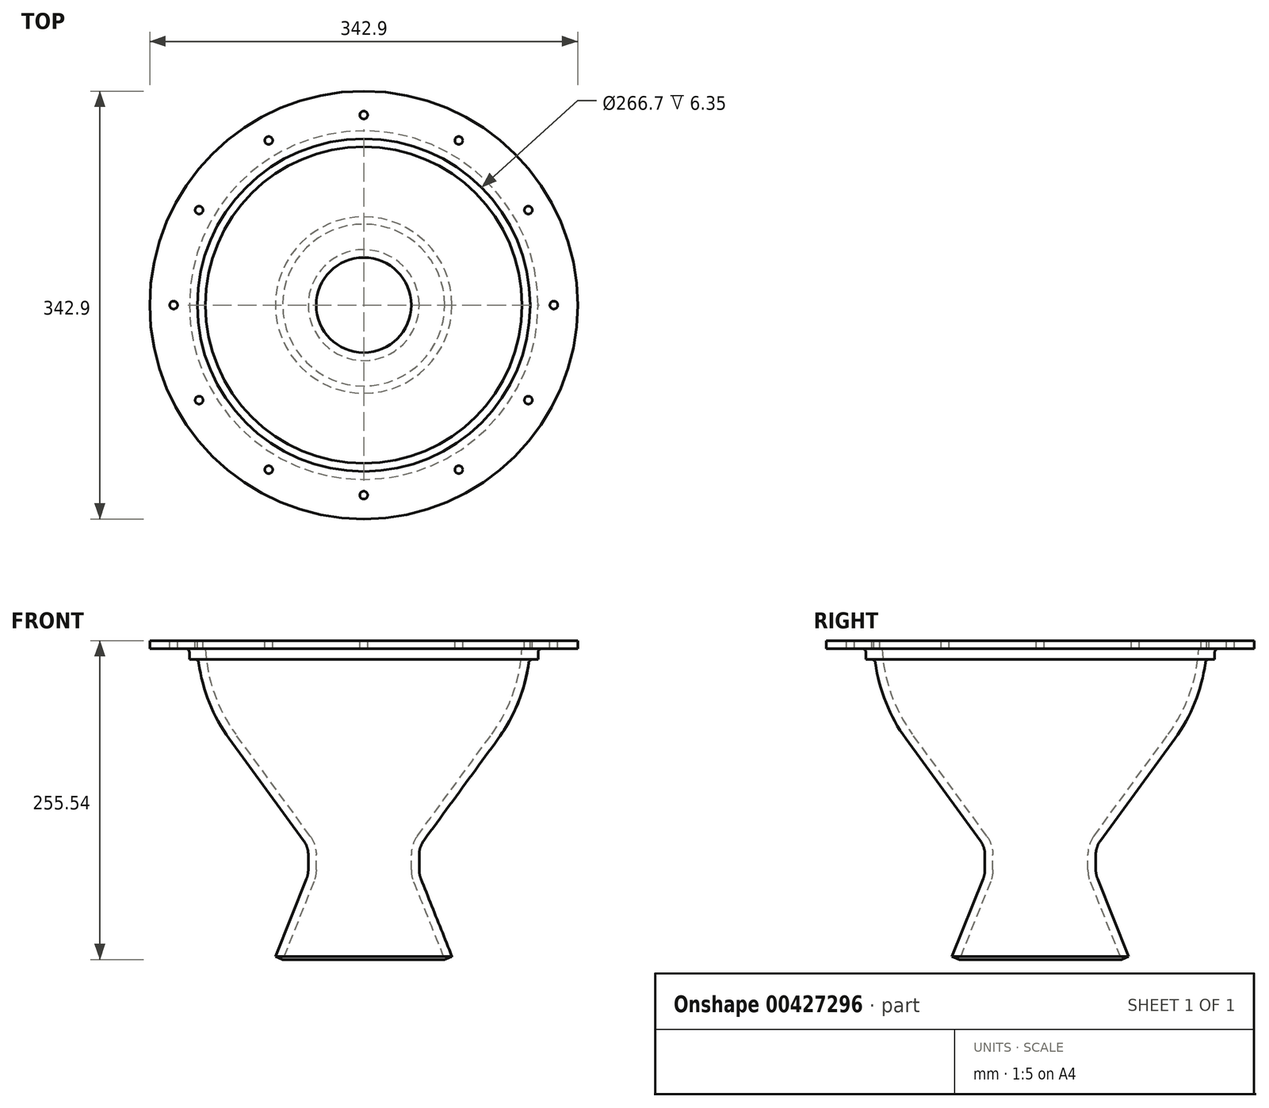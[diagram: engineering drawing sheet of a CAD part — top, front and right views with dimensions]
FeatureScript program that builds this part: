
annotation { "Feature Type Name" : "Feature", "Feature Type Description" : "" }
export const myFeature = defineFeature(function(context is Context, id is Id, definition is map)
    precondition{}
    {
        {
            var Q0;
            Q0=qCreatedBy(makeId("Front.planeOp"),FACE);
            var sketch = newSketch(context, id + "F0", { "sketchPlane" : qUnion([Q0])});
            skArc(sketch, "E0", {"start": v(127, 0) * mm, "mid": v(89.8, 89.8) * mm, "end": v(0, 127) * mm});
            skLineSegment(sketch, "E1", {"start": v(127, 0) * mm, "end": v(127, -6.35) * mm});
            skLineSegment(sketch, "E2", {"start": v(127, -6.35) * mm, "end": v(133.35, -6.35) * mm});
            skLineSegment(sketch, "E3", {"start": v(133.35, -6.35) * mm, "end": v(133.35, 0) * mm});
            skLineSegment(sketch, "E4", {"start": v(133.35, 0) * mm, "end": v(133.35, 0) * mm});
            skLineSegment(sketch, "E5", {"start": v(171.45, 6.35) * mm, "end": v(133.2, 6.35) * mm});
            skArc(sketch, "E6.0", {"start": v(133.2, 6.35) * mm, "mid": v(92.02, 96.51) * mm, "end": v(0, 133.35) * mm});
            skLineSegment(sketch, "E7", {"start": v(0, 127) * mm, "end": v(0, 133.35) * mm});
            skPoint(sketch, "E8.end.orphan", {"position": v(-133.35, 0) * mm});
            skLineSegment(sketch, "E9", {"start": v(0, 0) * mm, "end": v(0, 26.63) * mm, "construction": true});
            skLineSegment(sketch, "E10", {"start": v(133.35, 0) * mm, "end": v(171.45, 0) * mm});
            skLineSegment(sketch, "E11", {"start": v(171.45, 0) * mm, "end": v(171.45, 6.35) * mm});
            skSolve(sketch);
        }
        {
            var Q0;
            Q0=makeQuery(id+"F0.imprint","IMPRINT",FACE,{"disambiguationData":[TD([[makeQuery(id+"F0.imprint","IMPRINT",EDGE,{"derivedFrom":sQuery(id+"F0.wireOp",EDGE,"E0")}),-1.0]])]});
            var Q1;
            Q1=sQuery(id+"F0.wireOp",EDGE,"E9");
            revolve(context, id + "F1", {"entities" : qUnion([Q0]), "axis" : qUnion([Q1]), "revolveType" : RevolveType.FULL});
        }
        {
            var Q0;
            Q0=qCreatedBy(makeId("Front.planeOp"),FACE);
            var sketch = newSketch(context, id + "F2", { "sketchPlane" : qUnion([Q0])});
            skLineSegment(sketch, "E12", {"start": v(0, 0) * mm, "end": v(0, 155.52) * mm});
            skLineSegment(sketch, "E13", {"start": v(0, 0) * mm, "end": v(109.2, 109.2) * mm});
            skSolve(sketch);
        }
        {
            var Q0;
            Q0=qCreatedBy(makeId("Top.planeOp"),FACE);
            var Q1;
            Q1=sQuery(id+"F2.wireOp",EDGE,"E13");
            cPlane(context, id + "F3", {"entities" : qUnion([Q0, Q1]), "cplaneType" : CPlaneType.LINE_ANGLE, "offset" : 25.4 * mm, "angle" : 0 * degree, "oppositeDirection" : true, "width" : 152.4 * mm, "height" : 152.4 * mm});
        }
        {
            var Q0;
            Q0=qCreatedBy(makeId("Front.planeOp"),FACE);
            var sketch = newSketch(context, id + "F4", { "sketchPlane" : qUnion([Q0])});
            skArc(sketch, "E14", {"start": v(98.33, 80.37) * mm, "mid": v(94.19, 85.2) * mm, "end": v(89.8, 89.8) * mm});
            skLineSegment(sketch, "E15", {"start": v(89.8, 89.8) * mm, "end": v(94.3, 94.3) * mm});
            skLineSegment(sketch, "E16", {"start": v(0, 0) * mm, "end": v(0, 157.57) * mm});
            skLineSegment(sketch, "E17.0", {"start": v(98.33, 80.37) * mm, "end": v(100.78, 82.81) * mm});
            skLineSegment(sketch, "E18", {"start": v(103.02, 80.57) * mm, "end": v(100.78, 82.81) * mm});
            skLineSegment(sketch, "E19", {"start": v(103.02, 80.57) * mm, "end": v(110.36, 87.91) * mm});
            skPoint(sketch, "E20.trimOffspring.end.orphan", {"position": v(-133.2, 6.35) * mm});
            skPoint(sketch, "E21.trimOffspring.end.orphan", {"position": v(-127, 0) * mm});
            skPoint(sketch, "E22.start.orphan", {"position": v(133.2, 6.35) * mm});
            skLineSegment(sketch, "E23", {"start": v(94.3, 94.3) * mm, "end": v(110.36, 87.91) * mm});
            skPoint(sketch, "E24.orphan", {"position": v(127, 0) * mm});
            skSolve(sketch);
        }
        {
            var Q0;
            Q0=makeQuery(id+"F4.imprint","IMPRINT",FACE,{"disambiguationData":[TD([[makeQuery(id+"F4.imprint","IMPRINT",EDGE,{"derivedFrom":sQuery(id+"F4.wireOp",EDGE,"E14")}),-1.0]])]});
            var Q1;
            Q1=sQuery(id+"F4.wireOp",EDGE,"E15");
            revolve(context, id + "F5", {"operationType" : NewBodyOperationType.REMOVE, "entities" : qUnion([Q0]), "axis" : qUnion([Q1]), "revolveType" : RevolveType.FULL, "oppositeDirection" : true});
        }
        {
            var Q0;
            Q0=qCreatedBy(makeId("Front.planeOp"),FACE);
            var sketch = newSketch(context, id + "F6", { "sketchPlane" : qUnion([Q0])});
            skLineSegment(sketch, "E25", {"start": v(0, 127) * mm, "end": v(0, 133.35) * mm});
            skArc(sketch, "E26", {"start": v(0, 133.35) * mm, "mid": v(-3.97, 133.3) * mm, "end": v(-7.94, 133.11) * mm});
            skArc(sketch, "E27", {"start": v(-104.85, 82.4) * mm, "mid": v(-124.95, 46.58) * mm, "end": v(-133.2, 6.35) * mm});
            skArc(sketch, "E28", {"start": v(133.2, 6.35) * mm, "mid": v(124.95, 46.58) * mm, "end": v(104.85, 82.4) * mm});
            skArc(sketch, "E29", {"start": v(0, 127) * mm, "mid": v(-3.97, 126.94) * mm, "end": v(-7.94, 126.75) * mm});
            skArc(sketch, "E30", {"start": v(-98.33, 80.37) * mm, "mid": v(-119.62, 42.67) * mm, "end": v(-127, 0) * mm});
            skArc(sketch, "E31", {"start": v(127, 0) * mm, "mid": v(119.62, 42.67) * mm, "end": v(98.33, 80.37) * mm});
            skLineSegment(sketch, "E32.0", {"start": v(-7.94, 126.75) * mm, "end": v(-7.94, 133.11) * mm});
            skPoint(sketch, "E33.orphan", {"position": v(80.37, 98.33) * mm});
            skPoint(sketch, "E34.orphan", {"position": v(82.4, 104.85) * mm});
            skPoint(sketch, "E35.orphan", {"position": v(-82.4, 104.85) * mm});
            skPoint(sketch, "E36.orphan", {"position": v(-80.37, 98.33) * mm});
            skSolve(sketch);
        }
        {
            var Q0;
            Q0=makeQuery(id+"F6.imprint","IMPRINT",FACE,{"disambiguationData":[TD([[makeQuery(id+"F6.imprint","IMPRINT",EDGE,{"derivedFrom":sQuery(id+"F6.wireOp",EDGE,"E25")}),1.0]])]});
            var Q1;
            Q1=sQuery(id+"F6.wireOp",EDGE,"E25");
            revolve(context, id + "F7", {"operationType" : NewBodyOperationType.REMOVE, "entities" : qUnion([Q0]), "axis" : qUnion([Q1]), "revolveType" : RevolveType.FULL, "oppositeDirection" : true});
        }
        {
            var Q0;
            Q0=makeQuery(id+"F1.opRevolve","SWEPT_FACE",FACE,{"disambiguationData":[OSD([sQuery(id+"F0.wireOp",EDGE,"E5")])]});
            var sketch = newSketch(context, id + "F8", { "sketchPlane" : qUnion([Q0])});
            skLineSegment(sketch, "E37", {"start": v(0, -133.2) * mm, "end": v(0, -171.45) * mm, "construction": true});
            skCircle(sketch, "E38", {"center": v(0, 0) * mm, "radius": 171.45 * mm, "construction": true});
            skCircle(sketch, "E39", {"center": v(0, 0) * mm, "radius": 133.2 * mm, "construction": true});
            skPoint(sketch, "E40", {"position": v(0, -152.32) * mm});
            skSolve(sketch);
        }
        {
            var Q0;
            Q0=sQuery(id+"F8.wireOp",VERTEX,"E40");
            var Q1;
            Q1=makeQuery(id+"F1.opRevolve","SWEPT_BODY",BODY,{"disambiguationData":[OSD([sQuery(id+"F0.wireOp",EDGE,"E0"),sQuery(id+"F0.wireOp",EDGE,"E1"),sQuery(id+"F0.wireOp",EDGE,"E2"),sQuery(id+"F0.wireOp",EDGE,"E3"),sQuery(id+"F0.wireOp",EDGE,"E5"),sQuery(id+"F0.wireOp",EDGE,"E6.0"),sQuery(id+"F0.wireOp",EDGE,"E7"),sQuery(id+"F0.wireOp",EDGE,"E10"),sQuery(id+"F0.wireOp",EDGE,"E11")])]});
            hole(context, id + "F9", {"style" : HoleStyle.SIMPLE, "endStyle" : HoleEndStyle.THROUGH, "holeDiameter" : 6.35 * mm, "isTappedThrough" : true, "tappedDepth" : 12.7 * mm, "tapClearance" : 3, "locations" : qUnion([Q0]), "scope" : qUnion([Q1])});
        }
        {
            var Q0;
            Q0=qCreatedBy(makeId("Front.planeOp"),FACE);
            var sketch = newSketch(context, id + "F10", { "sketchPlane" : qUnion([Q0])});
            skLineSegment(sketch, "E41", {"start": v(-171.45, 0) * mm, "end": v(-133.35, 0) * mm});
            skLineSegment(sketch, "E42", {"start": v(-133.35, -6.35) * mm, "end": v(-126.84, -6.35) * mm});
            skLineSegment(sketch, "E43", {"start": v(-133.35, 0) * mm, "end": v(-133.35, -6.35) * mm});
            skArc(sketch, "E44", {"start": v(-126.84, -6.35) * mm, "mid": v(-119.72, -42.38) * mm, "end": v(-102.59, -74.87) * mm});
            skLineSegment(sketch, "E45", {"start": v(-171.45, 0) * mm, "end": v(-171.45, -6.35) * mm});
            skPoint(sketch, "E46.end.orphan", {"position": v(-133.35, 0) * mm});
            skPoint(sketch, "E46.start.orphan", {"position": v(-149.15, 0) * mm});
            skPoint(sketch, "E47.orphan", {"position": v(-155.5, 0) * mm});
            skPoint(sketch, "E48.end.orphan", {"position": v(-80.37, 98.33) * mm});
            skPoint(sketch, "E48.start.orphan", {"position": v(-7.94, 126.75) * mm});
            skPoint(sketch, "E49.end.orphan", {"position": v(7.94, 126.75) * mm});
            skPoint(sketch, "E49.start.orphan", {"position": v(80.37, 98.33) * mm});
            skPoint(sketch, "E50.end.orphan", {"position": v(98.33, 80.37) * mm});
            skPoint(sketch, "E50.start.orphan", {"position": v(127, 0) * mm});
            skPoint(sketch, "E51.end.orphan", {"position": v(127, -6.35) * mm});
            skPoint(sketch, "E52.end.orphan", {"position": v(133.35, -6.35) * mm});
            skPoint(sketch, "E53.end.orphan", {"position": v(133.35, 0) * mm});
            skPoint(sketch, "E54.end.orphan", {"position": v(149.15, 0) * mm});
            skPoint(sketch, "E55.end.orphan", {"position": v(171.45, 0) * mm});
            skPoint(sketch, "E55.start.orphan", {"position": v(155.5, 0) * mm});
            skPoint(sketch, "E56.orphan", {"position": v(-127, 0) * mm});
            skPoint(sketch, "E57.orphan", {"position": v(-98.33, 80.37) * mm});
            skPoint(sketch, "E58.start.orphan", {"position": v(-127, -6.35) * mm});
            skLineSegment(sketch, "E59", {"start": v(-38.1, -183.74) * mm, "end": v(-38.1, -171.51) * mm});
            skPoint(sketch, "E60.visualSharp", {"position": v(-31.75, -122.97) * mm});
            skPoint(sketch, "E61.visualSharp", {"position": v(-44.5, -173.77) * mm});
            skPoint(sketch, "E62.start.orphan", {"position": v(-31.75, -186.47) * mm});
            skLineSegment(sketch, "E63", {"start": v(-42.98, -156.54) * mm, "end": v(-102.59, -74.87) * mm});
            skLineSegment(sketch, "E64", {"start": v(-39.92, -193.17) * mm, "end": v(-64.86, -255.54) * mm});
            skPoint(sketch, "E65.start.orphan", {"position": v(-31.75, -249.97) * mm});
            skPoint(sketch, "E66.visualSharp", {"position": v(-38.1, -163.23) * mm});
            skArc(sketch, "E66.filletArc", {"start": v(-38.1, -171.51) * mm, "mid": v(-39.35, -163.64) * mm, "end": v(-42.98, -156.54) * mm});
            skPoint(sketch, "E67.visualSharp", {"position": v(-38.1, -188.63) * mm});
            skArc(sketch, "E67.filletArc", {"start": v(-39.92, -193.17) * mm, "mid": v(-38.56, -188.54) * mm, "end": v(-38.1, -183.74) * mm});
            skPoint(sketch, "E68.0.end.orphan", {"position": v(6.35, -67.27) * mm});
            skLineSegment(sketch, "E69.0", {"start": v(-45.81, -190.82) * mm, "end": v(-70.76, -253.18) * mm});
            skArc(sketch, "E69.1", {"start": v(-45.81, -190.82) * mm, "mid": v(-44.8, -187.34) * mm, "end": v(-44.45, -183.74) * mm});
            skArc(sketch, "E69.2", {"start": v(-132.16, -17.8) * mm, "mid": v(-123.73, -49.73) * mm, "end": v(-107.72, -78.6) * mm});
            skLineSegment(sketch, "E69.3", {"start": v(-48.11, -160.28) * mm, "end": v(-107.72, -78.6) * mm});
            skArc(sketch, "E69.4", {"start": v(-44.45, -171.51) * mm, "mid": v(-45.39, -165.6) * mm, "end": v(-48.11, -160.28) * mm});
            skLineSegment(sketch, "E69.5", {"start": v(-44.45, -183.74) * mm, "end": v(-44.45, -171.51) * mm});
            skLineSegment(sketch, "E70", {"start": v(-64.86, -255.54) * mm, "end": v(-70.76, -253.18) * mm});
            skLineSegment(sketch, "E71", {"start": v(-171.45, -6.35) * mm, "end": v(-142.88, -6.35) * mm});
            skLineSegment(sketch, "E72", {"start": v(-139.7, -9.52) * mm, "end": v(-139.7, -15.06) * mm});
            skLineSegment(sketch, "E73", {"start": v(-139.7, -15.06) * mm, "end": v(-135.3, -15.06) * mm});
            skPoint(sketch, "E74.visualSharp", {"position": v(-139.7, -6.35) * mm});
            skArc(sketch, "E74.filletArc", {"start": v(-139.7, -9.52) * mm, "mid": v(-140.63, -7.28) * mm, "end": v(-142.88, -6.35) * mm});
            skPoint(sketch, "E75.visualSharp", {"position": v(-132.5, -15.06) * mm});
            skArc(sketch, "E75.filletArc", {"start": v(-132.16, -17.8) * mm, "mid": v(-133.21, -15.84) * mm, "end": v(-135.3, -15.06) * mm});
            skLineSegment(sketch, "E76", {"start": v(0, 0) * mm, "end": v(0, -104.7) * mm});
            skSolve(sketch);
        }
        {
            var Q0;
            Q0=makeQuery(id+"F10.imprint","IMPRINT",FACE,{"disambiguationData":[TD([[makeQuery(id+"F10.imprint","IMPRINT",EDGE,{"derivedFrom":sQuery(id+"F10.wireOp",EDGE,"E41")}),-1.0]])]});
            var Q1;
            Q1=sQuery(id+"F10.wireOp",EDGE,"E76");
            revolve(context, id + "F11", {"entities" : qUnion([Q0]), "axis" : qUnion([Q1]), "revolveType" : RevolveType.FULL});
        }
        {
            var Q0;
            Q0=makeQuery(id+"F11.opRevolve","SWEPT_FACE",FACE,{"disambiguationData":[OSD([sQuery(id+"F10.wireOp",EDGE,"E41")])]});
            var sketch = newSketch(context, id + "F12", { "sketchPlane" : qUnion([Q0])});
            skCircle(sketch, "E77.0", {"center": v(131.92, -76.16) * mm, "radius": 3.17 * mm});
            skCircle(sketch, "E78.0", {"center": v(131.92, 76.16) * mm, "radius": 3.17 * mm});
            skCircle(sketch, "E79.0", {"center": v(76.16, 131.92) * mm, "radius": 3.18 * mm});
            skCircle(sketch, "E80.0", {"center": v(0, 152.32) * mm, "radius": 3.18 * mm});
            skCircle(sketch, "E81.0", {"center": v(-76.16, 131.92) * mm, "radius": 3.18 * mm});
            skCircle(sketch, "E82.0", {"center": v(-131.92, 76.16) * mm, "radius": 3.17 * mm});
            skCircle(sketch, "E83.0", {"center": v(-152.32, 0) * mm, "radius": 3.18 * mm});
            skCircle(sketch, "E84.0", {"center": v(-131.92, -76.16) * mm, "radius": 3.17 * mm});
            skCircle(sketch, "E85.0", {"center": v(-76.16, -131.92) * mm, "radius": 3.18 * mm});
            skCircle(sketch, "E86.0", {"center": v(0, -152.32) * mm, "radius": 3.18 * mm});
            skCircle(sketch, "E87.0", {"center": v(76.16, -131.92) * mm, "radius": 3.18 * mm});
            skCircle(sketch, "E88.0", {"center": v(152.32, 0) * mm, "radius": 3.18 * mm});
            skSolve(sketch);
        }
        {
            var Q0;
            Q0=makeQuery(id+"F12.imprint","IMPRINT",FACE,{"disambiguationData":[TD([[makeQuery(id+"F12.imprint","IMPRINT",EDGE,{"derivedFrom":sQuery(id+"F12.wireOp",EDGE,"E86.0")}),1.0]])]});
            var Q1;
            Q1=makeQuery(id+"F12.imprint","IMPRINT",FACE,{"disambiguationData":[TD([[makeQuery(id+"F12.imprint","IMPRINT",EDGE,{"derivedFrom":sQuery(id+"F12.wireOp",EDGE,"E87.0")}),1.0]])]});
            var Q2;
            Q2=makeQuery(id+"F12.imprint","IMPRINT",FACE,{"disambiguationData":[TD([[makeQuery(id+"F12.imprint","IMPRINT",EDGE,{"derivedFrom":sQuery(id+"F12.wireOp",EDGE,"E77.0")}),1.0]])]});
            var Q3;
            Q3=makeQuery(id+"F12.imprint","IMPRINT",FACE,{"disambiguationData":[TD([[makeQuery(id+"F12.imprint","IMPRINT",EDGE,{"derivedFrom":sQuery(id+"F12.wireOp",EDGE,"E88.0")}),1.0]])]});
            var Q4;
            Q4=makeQuery(id+"F12.imprint","IMPRINT",FACE,{"disambiguationData":[TD([[makeQuery(id+"F12.imprint","IMPRINT",EDGE,{"derivedFrom":sQuery(id+"F12.wireOp",EDGE,"E78.0")}),1.0]])]});
            var Q5;
            Q5=makeQuery(id+"F12.imprint","IMPRINT",FACE,{"disambiguationData":[TD([[makeQuery(id+"F12.imprint","IMPRINT",EDGE,{"derivedFrom":sQuery(id+"F12.wireOp",EDGE,"E79.0")}),1.0]])]});
            var Q6;
            Q6=makeQuery(id+"F12.imprint","IMPRINT",FACE,{"disambiguationData":[TD([[makeQuery(id+"F12.imprint","IMPRINT",EDGE,{"derivedFrom":sQuery(id+"F12.wireOp",EDGE,"E80.0")}),1.0]])]});
            var Q7;
            Q7=makeQuery(id+"F12.imprint","IMPRINT",FACE,{"disambiguationData":[TD([[makeQuery(id+"F12.imprint","IMPRINT",EDGE,{"derivedFrom":sQuery(id+"F12.wireOp",EDGE,"E81.0")}),1.0]])]});
            var Q8;
            Q8=makeQuery(id+"F12.imprint","IMPRINT",FACE,{"disambiguationData":[TD([[makeQuery(id+"F12.imprint","IMPRINT",EDGE,{"derivedFrom":sQuery(id+"F12.wireOp",EDGE,"E82.0")}),1.0]])]});
            var Q9;
            Q9=makeQuery(id+"F12.imprint","IMPRINT",FACE,{"disambiguationData":[TD([[makeQuery(id+"F12.imprint","IMPRINT",EDGE,{"derivedFrom":sQuery(id+"F12.wireOp",EDGE,"E83.0")}),1.0]])]});
            var Q10;
            Q10=makeQuery(id+"F12.imprint","IMPRINT",FACE,{"disambiguationData":[TD([[makeQuery(id+"F12.imprint","IMPRINT",EDGE,{"derivedFrom":sQuery(id+"F12.wireOp",EDGE,"E84.0")}),1.0]])]});
            var Q11;
            Q11=makeQuery(id+"F12.imprint","IMPRINT",FACE,{"disambiguationData":[TD([[makeQuery(id+"F12.imprint","IMPRINT",EDGE,{"derivedFrom":sQuery(id+"F12.wireOp",EDGE,"E85.0")}),1.0]])]});
            extrude(context, id + "F13", {"entities" : qUnion([Q0, Q1, Q2, Q3, Q4, Q5, Q6, Q7, Q8, Q9, Q10, Q11]), "operationType" : NewBodyOperationType.REMOVE, "oppositeDirection" : true, "depth" : 25.4 * mm});
        }
        {
            var Q0;
            Q0=makeQuery(id+"F1.opRevolve","SWEPT_BODY",BODY,{"disambiguationData":[OSD([sQuery(id+"F0.wireOp",EDGE,"E0"),sQuery(id+"F0.wireOp",EDGE,"E1"),sQuery(id+"F0.wireOp",EDGE,"E2"),sQuery(id+"F0.wireOp",EDGE,"E3"),sQuery(id+"F0.wireOp",EDGE,"E5"),sQuery(id+"F0.wireOp",EDGE,"E6.0"),sQuery(id+"F0.wireOp",EDGE,"E7"),sQuery(id+"F0.wireOp",EDGE,"E10"),sQuery(id+"F0.wireOp",EDGE,"E11")])]});
            deleteBodies(context, id + "F14", {"entities" : qUnion([Q0])});
        }
    });
